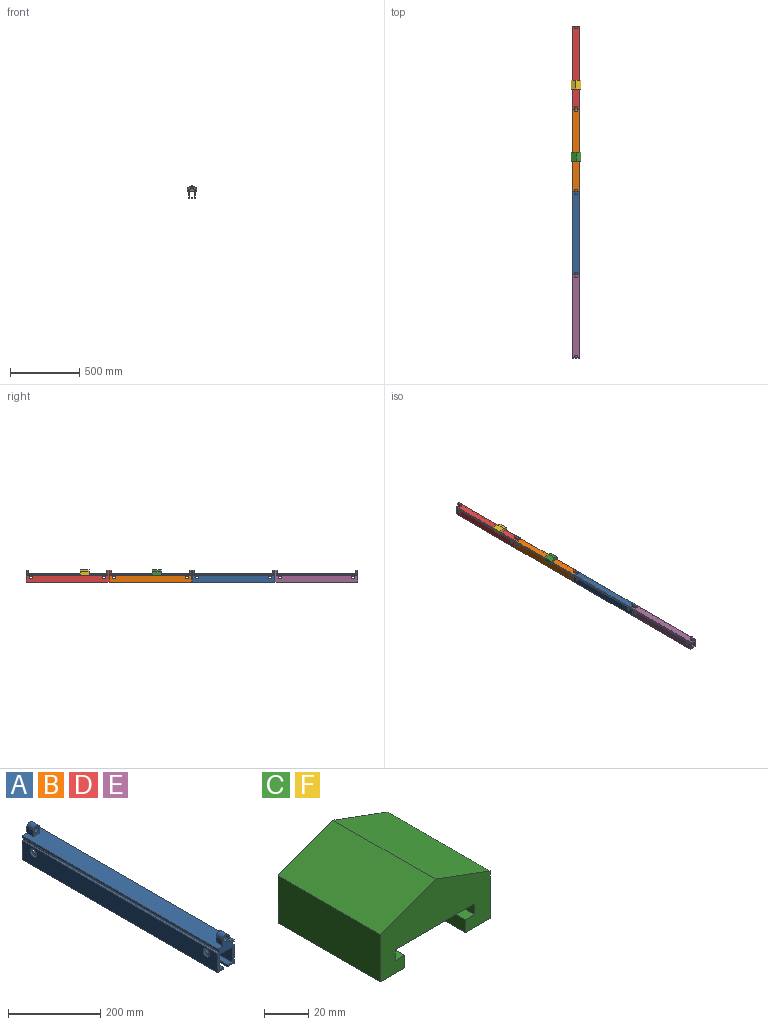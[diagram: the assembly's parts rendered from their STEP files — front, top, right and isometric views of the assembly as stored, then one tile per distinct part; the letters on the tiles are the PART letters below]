
ASSEMBLY  parts=6 mates=5
PART A: 36 faces, bbox 50x600x88 mm
  f0: plane 600x50mm, normal (0,0,1), area 29200mm2, adj f7,f10,f19,f20,f27,f28,f29,f32
  f1: plane 600x50mm, normal (1,0,0), area 29371.7mm2, adj f7,f8,f9,f10,f24,f25
  f2: plane 600x50mm, normal (-1,0,0), area 29371.7mm2, adj f5,f6,f7,f10,f22,f23
  f3: plane 600x40mm, normal (-1,0,0), area 23371.7mm2, adj f7,f10,f11,f13,f24,f25
  f4: plane 600x40mm, normal (1,0,0), area 23371.7mm2, adj f7,f10,f11,f12,f22,f23
  f5: plane 600x5.81mm, normal (0,0,1), area 3484.7mm2, adj f2,f7,f10,f16
  f6: plane 600x18.81mm, normal (0,0,-1), area 11284.7mm2, adj f2,f7,f10,f14
  f7: plane 88x50mm, normal (0,1,0), area 1740.1mm2, adj f0,f1,f2,f3,f4,f5,f6,f8
  f8: plane 600x18.81mm, normal (0,0,-1), area 11284.7mm2, adj f1,f7,f10,f15
  f9: plane 600x5.81mm, normal (0,0,1), area 3484.7mm2, adj f1,f7,f10,f17
  f10: plane 88x50mm, normal (0,-1,0), area 1740.1mm2, adj f0,f1,f2,f3,f4,f5,f6,f8
  f11: plane 600x38.38mm, normal (0,0,-1), area 23030.7mm2, adj f3,f4,f7,f10
  f12: plane 600x13mm, normal (0,0,1), area 7800mm2, adj f4,f7,f10,f14
  f13: plane 600x13mm, normal (0,0,1), area 7800mm2, adj f3,f7,f10,f15
  f14: plane 600x5mm, normal (1,0,0), area 3000mm2, adj f6,f7,f10,f12
  f15: plane 600x5mm, normal (-1,0,0), area 3000mm2, adj f7,f8,f10,f13
  f16: plane 600x8mm, normal (-1,0,0), area 4800mm2, adj f5,f7,f10,f21
  f17: plane 600x8mm, normal (1,0,0), area 4800mm2, adj f7,f9,f10,f18
  f18: plane 600x5.81mm, normal (0,0,-1), area 3484.7mm2, adj f7,f10,f17,f19
  f19: plane 600x5mm, normal (1,0,0), area 3000mm2, adj f0,f7,f10,f18
  f20: plane 600x5mm, normal (-1,0,0), area 3000mm2, adj f0,f7,f10,f21
  f21: plane 600x5.81mm, normal (0,0,-1), area 3484.7mm2, adj f7,f10,f16,f20
  f22: cylinder r=10mm len=20mm, axis (1,0,0), area 364.9mm2, adj f2,f4
  f23: cylinder r=10mm len=20mm, axis (1,0,0), area 364.9mm2, adj f2,f4
  f24: cylinder r=10mm len=20mm, axis (1,0,0), area 364.9mm2, adj f1,f3
  f25: cylinder r=10mm len=20mm, axis (1,0,0), area 364.9mm2, adj f1,f3
  f26: cylinder r=10mm len=20mm, axis (0,1,0), area 628.3mm2, adj f7,f27,f28,f29
  f27: plane 20x15mm, normal (1,0,0), area 300mm2, adj f0,f7,f26,f29
  f28: plane 20x15mm, normal (-1,0,0), area 300mm2, adj f0,f7,f26,f29
  f29: plane 25x20mm, normal (0,-1,0), area 280.4mm2, adj f0,f26,f27,f28,f30
  f30: cylinder r=7.5mm len=20mm, axis (0,1,0), area 942.5mm2, adj f7,f29
  f31: cylinder r=10mm len=20mm, axis (0,-1,0), area 628.3mm2, adj f10,f32,f33,f34
  f32: plane 20x15mm, normal (1,0,0), area 300mm2, adj f0,f10,f31,f34
  f33: plane 20x15mm, normal (-1,0,0), area 300mm2, adj f0,f10,f31,f34
  f34: plane 25x20mm, normal (0,1,0), area 280.4mm2, adj f0,f31,f32,f33,f35
  f35: cylinder r=7.5mm len=20mm, axis (0,-1,0), area 942.5mm2, adj f10,f34
PART B: same geometry as A
PART C: 15 faces, bbox 70x65x39.2 mm
  f0: plane 65x6mm, normal (1,0,0), area 390mm2, adj f1,f10,f11,f12
  f1: plane 65x50.85mm, normal (0,0,-1), area 3305.2mm2, adj f0,f2,f11,f12
  f2: plane 65x6mm, normal (-1,0,0), area 390mm2, adj f1,f3,f11,f12
  f3: plane 65x6mm, normal (0,0,1), area 390mm2, adj f2,f4,f11,f12
  f4: plane 65x7mm, normal (-1,0,0), area 455mm2, adj f3,f5,f11,f12
  f5: plane 65x15.58mm, normal (0,0,-1), area 1012.4mm2, adj f4,f6,f11,f12
  f6: plane 65x26.24mm, normal (1,0,0), area 1705.9mm2, adj f5,f11,f12,f13
  f7: plane 65x25.99mm, normal (-1,0,0), area 1689.4mm2, adj f8,f11,f12,f14
  f8: plane 65x15.58mm, normal (0,0,-1), area 1012.4mm2, adj f7,f9,f11,f12
  f9: plane 65x7mm, normal (1,0,0), area 455mm2, adj f8,f10,f11,f12
  f10: plane 65x6mm, normal (0,0,1), area 390mm2, adj f0,f9,f11,f12
  f11: plane 70x39.22mm, normal (0,-1,0), area 1709.6mm2, adj f0,f1,f2,f3,f4,f5,f6,f7
  f12: plane 70x39.22mm, normal (0,1,0), area 1709.6mm2, adj f0,f1,f2,f3,f4,f5,f6,f7
  f13: plane 65x35mm, normal (0.35,0,0.94), area 2426.2mm2, adj f6,f11,f12,f14
  f14: plane 65x35mm, normal (-0.35,0,0.94), area 2432mm2, adj f7,f11,f12,f13
PART D: same geometry as A
PART E: same geometry as A
PART F: same geometry as C
PLACE A t=(-211.93,-467.56,-109.36)mm
PLACE B t=(-211.93,132.44,-109.36)mm
PLACE C t=(-211.9,-181.69,-61.26)mm
PLACE D t=(-211.93,732.44,-109.36)mm
PLACE E t=(-211.93,-1067.56,-109.36)mm
PLACE F t=(-212.17,341.22,-61.46)mm
MATE fastened A.f7 <-> B.f10  axis (0,1,0) through (-229.43,-467.56,-71.36)mm
MATE fastened D.f10 <-> B.f7  axis (0,-1,0) through (-229.43,132.44,-71.36)mm
MATE slider C.f11 <-> B.f10  axis (0,1,0) through (-231.32,-246.69,-83.76)mm
MATE fastened E.f7 <-> A.f10  axis (0,1,0) through (-229.43,-1067.56,-71.36)mm
MATE slider F.f12 <-> D.f7  axis (0,1,0) through (-192.74,341.22,-83.96)mm
